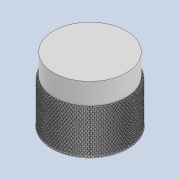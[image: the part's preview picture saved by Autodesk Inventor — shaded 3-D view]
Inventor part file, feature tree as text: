
AUTODESK INVENTOR PART (.ipt)
format: ipt  version: 2021 (Build 250183000, 183)  size: 12,340,224 bytes
history: native  units: mm
features: extrude x3, sketch x2, helix x2, pattern_circular x2, fillet x1
ambient origin geometry x8: Origin, YZ Plane, XZ Plane, XY Plane, X Axis, Y Axis, Z Axis, Center Point
bodies: Solid1 (feature_tree)
feature tree (10):
  sketch  "Sketch1"  dims[d0=18.0mm d1=15.0mm d2=0.0mm]
  extrude  "Extrusion1"  Depth=15.0mm
  helix  "Coil1"  [1 undecoded]
  pattern_circular  "Circular Pattern1"  [2 undecoded]
  helix  "Coil2"  [1 undecoded]
  pattern_circular  "Circular Pattern2"  [2 undecoded]
  extrude  "Extrusion2"  TaperAngle=360.0deg  [1 undecoded]
  extrude  "Extrusion3"  Depth=0.5mm
  fillet  "Fillet1"  Radius=1.25mm
  sketch  "Sketch2"  dims[d3=0.698132mm d4=0.5mm d5=10.0mm d6=10.0mm d7=1.25mm d8=0.0mm d9=90.0deg d10=90.0deg d11=0.0mm d12=0.0mm d13=900.0mm d14=360.0deg d16=10.0mm d17=10.0mm d18=1.25mm d19=0.0mm d20=90.0deg d21=90.0deg d22=0.0mm d23=0.0mm d24=900.0mm d25=360.0deg d27=17.0mm d28=5.0mm d29=0.0mm d30=0.5mm d31=0.0mm d32=0.5mm]
note: 7 required parameter values undecoded (feature->parameter linkage not recoverable at this tier; creation-order binding heuristic only, values carry confidence <= 0.55)
